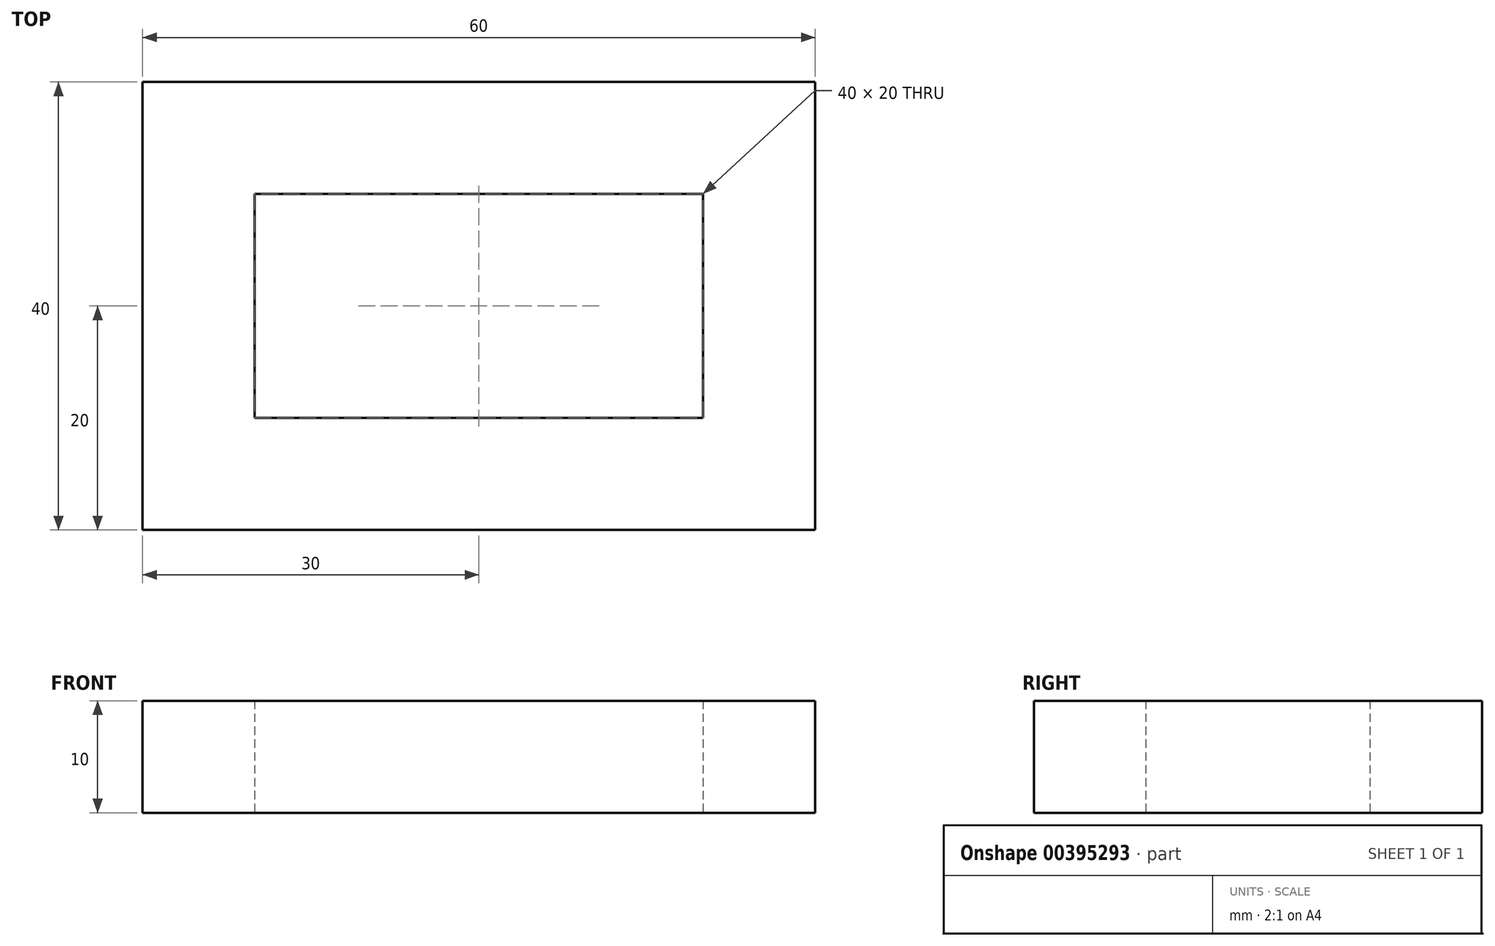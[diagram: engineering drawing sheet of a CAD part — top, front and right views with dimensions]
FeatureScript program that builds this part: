
annotation { "Feature Type Name" : "Feature", "Feature Type Description" : "" }
export const myFeature = defineFeature(function(context is Context, id is Id, definition is map)
    precondition{}
    {
        {
            var Q0;
            Q0=qCreatedBy(makeId("Top.planeOp"),FACE);
            var sketch = newSketch(context, id + "F0", { "sketchPlane" : qUnion([Q0])});
            skLineSegment(sketch, "E0.bottom", {"start": v(-30, 20) * mm, "end": v(30, 20) * mm});
            skLineSegment(sketch, "E0.top", {"start": v(-30, -20) * mm, "end": v(30, -20) * mm});
            skLineSegment(sketch, "E0.left", {"start": v(-30, 20) * mm, "end": v(-30, -20) * mm});
            skLineSegment(sketch, "E0.right", {"start": v(30, 20) * mm, "end": v(30, -20) * mm});
            skPoint(sketch, "E0.middle", {"position": v(0, 0) * mm});
            skLineSegment(sketch, "E1.bottom", {"start": v(-20, 10) * mm, "end": v(20, 10) * mm});
            skLineSegment(sketch, "E1.top", {"start": v(-20, -10) * mm, "end": v(20, -10) * mm});
            skLineSegment(sketch, "E1.left", {"start": v(-20, 10) * mm, "end": v(-20, -10) * mm});
            skLineSegment(sketch, "E1.right", {"start": v(20, 10) * mm, "end": v(20, -10) * mm});
            skSolve(sketch);
        }
        {
            var Q0;
            Q0 = qSketchRegion(id + "F0", true);
            extrude(context, id + "F1", {"entities" : qUnion([Q0]), "depth" : 10 * mm});
        }
    });
